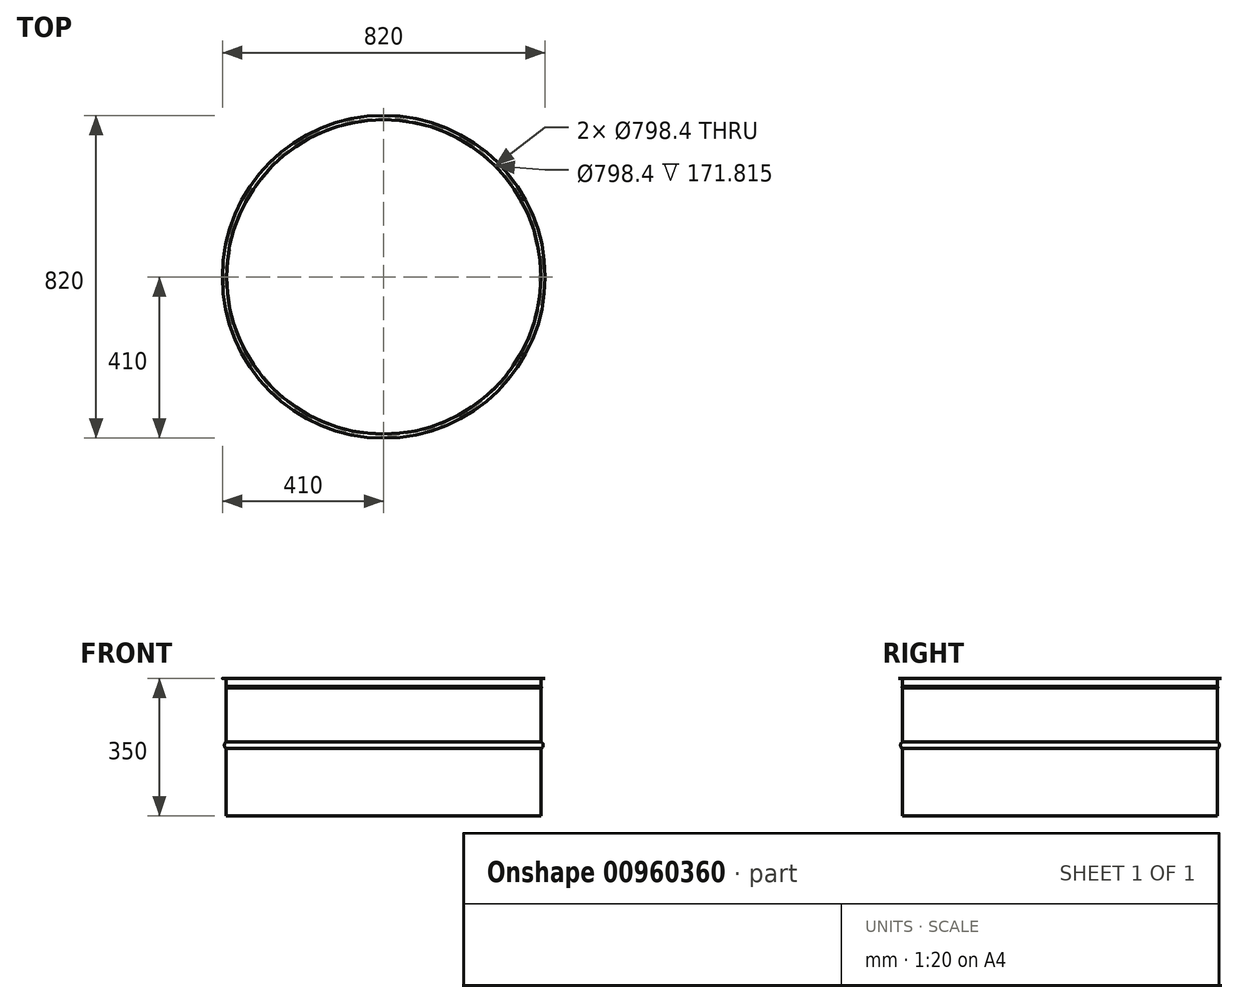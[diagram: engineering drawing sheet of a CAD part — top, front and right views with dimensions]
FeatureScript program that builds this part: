
annotation { "Feature Type Name" : "Feature", "Feature Type Description" : "" }
export const myFeature = defineFeature(function(context is Context, id is Id, definition is map)
    precondition{}
    {
        {
            var Q0;
            Q0=qCreatedBy(makeId("Front.planeOp"),FACE);
            var sketch = newSketch(context, id + "F0", { "sketchPlane" : qUnion([Q0])});
            skLineSegment(sketch, "E0", {"start": v(0, 0) * mm, "end": v(0, 350) * mm, "construction": true});
            skLineSegment(sketch, "E1", {"start": v(0, 350) * mm, "end": v(400, 350) * mm, "construction": true});
            skLineSegment(sketch, "E2", {"start": v(410, 350) * mm, "end": v(410, 349.2) * mm});
            skLineSegment(sketch, "E3", {"start": v(400, 0) * mm, "end": v(0, 0) * mm, "construction": true});
            skLineSegment(sketch, "E4", {"start": v(410, 349.2) * mm, "end": v(400.8, 349.2) * mm});
            skLineSegment(sketch, "E5", {"start": v(400, 348.4) * mm, "end": v(400, 328.73) * mm});
            skArc(sketch, "E6", {"start": v(400, 325.27) * mm, "mid": v(401, 327) * mm, "end": v(400, 328.73) * mm});
            skLineSegment(sketch, "E7.trimOffspring", {"start": v(400, 325.27) * mm, "end": v(400, 188.66) * mm});
            skArc(sketch, "E8", {"start": v(400, 171.34) * mm, "mid": v(405, 180) * mm, "end": v(400, 188.66) * mm});
            skLineSegment(sketch, "E9.trimOffspring", {"start": v(400, 171.34) * mm, "end": v(400, 0) * mm});
            skLineSegment(sketch, "E10", {"start": v(400, 349.2) * mm, "end": v(400, 350) * mm, "construction": true});
            skLineSegment(sketch, "E11.0", {"start": v(399.2, 171.81) * mm, "end": v(399.2, 0) * mm});
            skLineSegment(sketch, "E11.1", {"start": v(399.2, 348.4) * mm, "end": v(399.2, 328.18) * mm});
            skArc(sketch, "E11.2", {"start": v(399.2, 325.82) * mm, "mid": v(400.2, 327) * mm, "end": v(399.2, 328.18) * mm});
            skLineSegment(sketch, "E11.3", {"start": v(399.2, 325.82) * mm, "end": v(399.2, 188.19) * mm});
            skArc(sketch, "E11.4", {"start": v(399.2, 171.81) * mm, "mid": v(404.2, 180) * mm, "end": v(399.2, 188.19) * mm});
            skLineSegment(sketch, "E12", {"start": v(400.8, 350) * mm, "end": v(410, 350) * mm});
            skLineSegment(sketch, "E13", {"start": v(399.2, 0) * mm, "end": v(400, 0) * mm});
            skPoint(sketch, "E14.visualSharp", {"position": v(399.2, 350) * mm});
            skArc(sketch, "E14.filletArc", {"start": v(400.8, 350) * mm, "mid": v(399.67, 349.53) * mm, "end": v(399.2, 348.4) * mm});
            skPoint(sketch, "E15.visualSharp", {"position": v(400, 349.2) * mm});
            skArc(sketch, "E15.filletArc", {"start": v(400.8, 349.2) * mm, "mid": v(400.23, 348.97) * mm, "end": v(400, 348.4) * mm});
            skSolve(sketch);
        }
        {
            var Q0;
            Q0=makeQuery(id+"F0.imprint","IMPRINT",FACE,{"disambiguationData":[TD([[makeQuery(id+"F0.imprint","IMPRINT",EDGE,{"derivedFrom":sQuery(id+"F0.wireOp",EDGE,"E2")}),-1.0]])]});
            var Q1;
            Q1=sQuery(id+"F0.wireOp",EDGE,"E0");
            revolve(context, id + "F1", {"surfaceOperationType" : NewSurfaceOperationType.NEW, "entities" : qUnion([Q0]), "axis" : qUnion([Q1]), "revolveType" : RevolveType.FULL});
        }
    });
